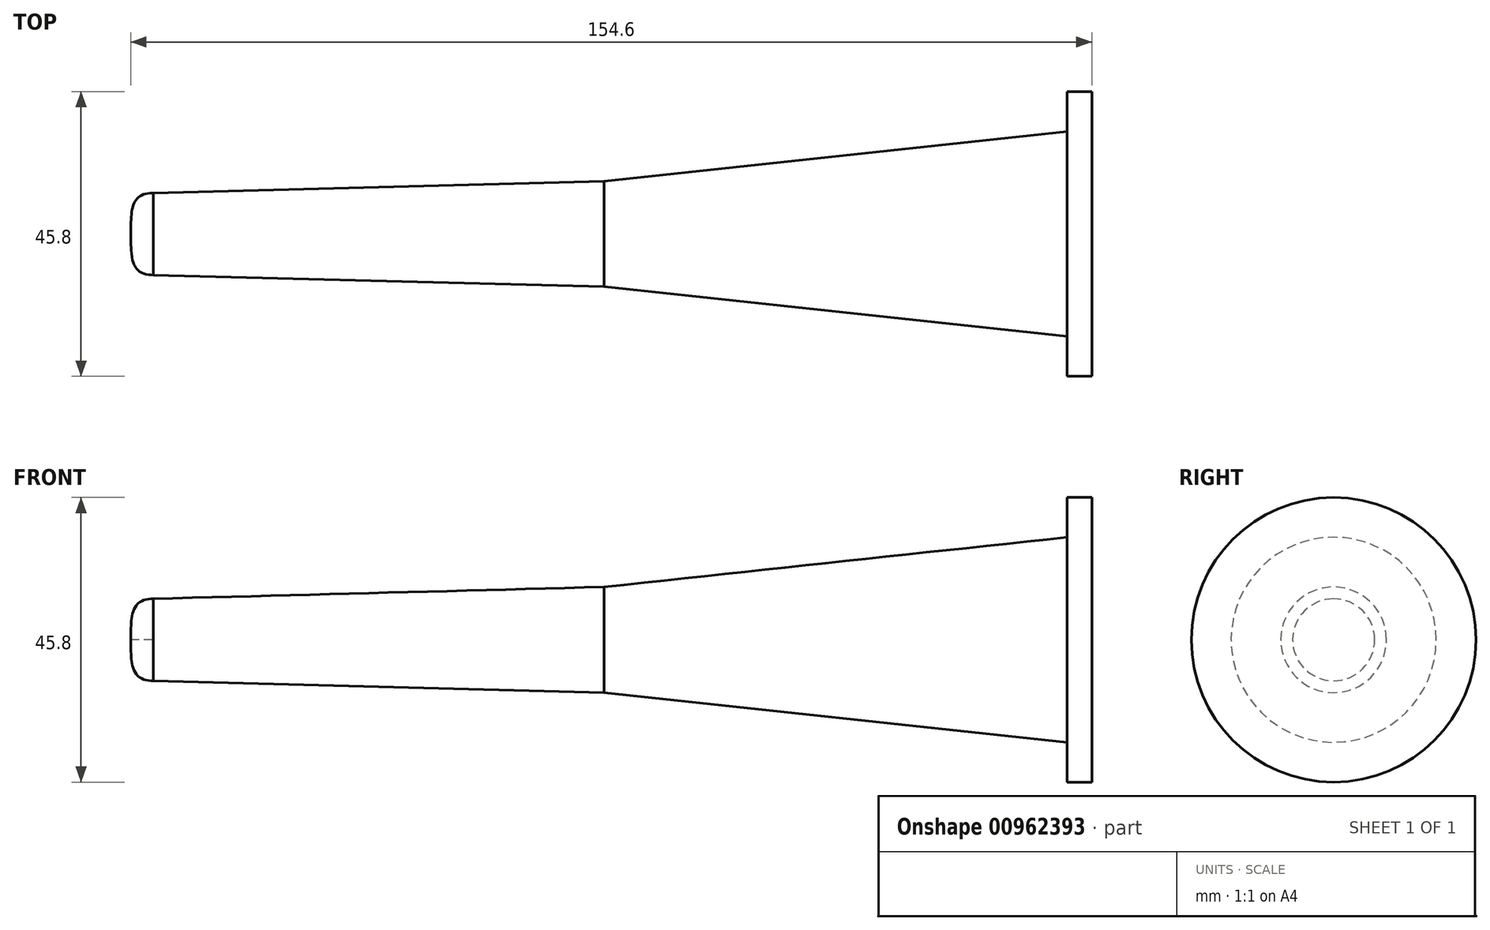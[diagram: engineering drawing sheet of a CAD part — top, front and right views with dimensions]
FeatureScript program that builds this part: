
annotation { "Feature Type Name" : "Feature", "Feature Type Description" : "" }
export const myFeature = defineFeature(function(context is Context, id is Id, definition is map)
    precondition{}
    {
        {
            var Q0;
            Q0=qCreatedBy(makeId("Top.planeOp"),FACE);
            var sketch = newSketch(context, id + "F0", { "sketchPlane" : qUnion([Q0])});
            skLineSegment(sketch, "E0", {"start": v(0, 0) * mm, "end": v(154.6, 0) * mm});
            skLineSegment(sketch, "E1", {"start": v(154.6, 0) * mm, "end": v(154.6, 22.9) * mm});
            skLineSegment(sketch, "E2", {"start": v(154.6, 22.9) * mm, "end": v(150.6, 22.9) * mm});
            skLineSegment(sketch, "E3", {"start": v(150.6, 22.9) * mm, "end": v(150.6, 16.5) * mm});
            skLineSegment(sketch, "E4", {"start": v(150.6, 16.5) * mm, "end": v(76.1, 8.5) * mm});
            skLineSegment(sketch, "E5", {"start": v(76.1, 8.5) * mm, "end": v(3.6, 6.6) * mm});
            skFitSpline(sketch, "E6", {"points": [v(3.6, 6.6) * mm, v(0, 0) * mm], "startDerivative": vector(-10.8, 0) * mm, "endDerivative": vector(0, -11.64) * mm});
            skSolve(sketch);
        }
        {
            var Q0;
            Q0=makeQuery(id+"F0.imprint","IMPRINT",FACE,{"disambiguationData":[TD([[makeQuery(id+"F0.imprint","IMPRINT",EDGE,{"derivedFrom":sQuery(id+"F0.wireOp",EDGE,"E0")}),1.0]])]});
            var Q1;
            Q1=sQuery(id+"F0.wireOp",EDGE,"E0");
            revolve(context, id + "F1", {"surfaceOperationType" : NewSurfaceOperationType.NEW, "entities" : qUnion([Q0]), "axis" : qUnion([Q1]), "revolveType" : RevolveType.FULL});
        }
    });
